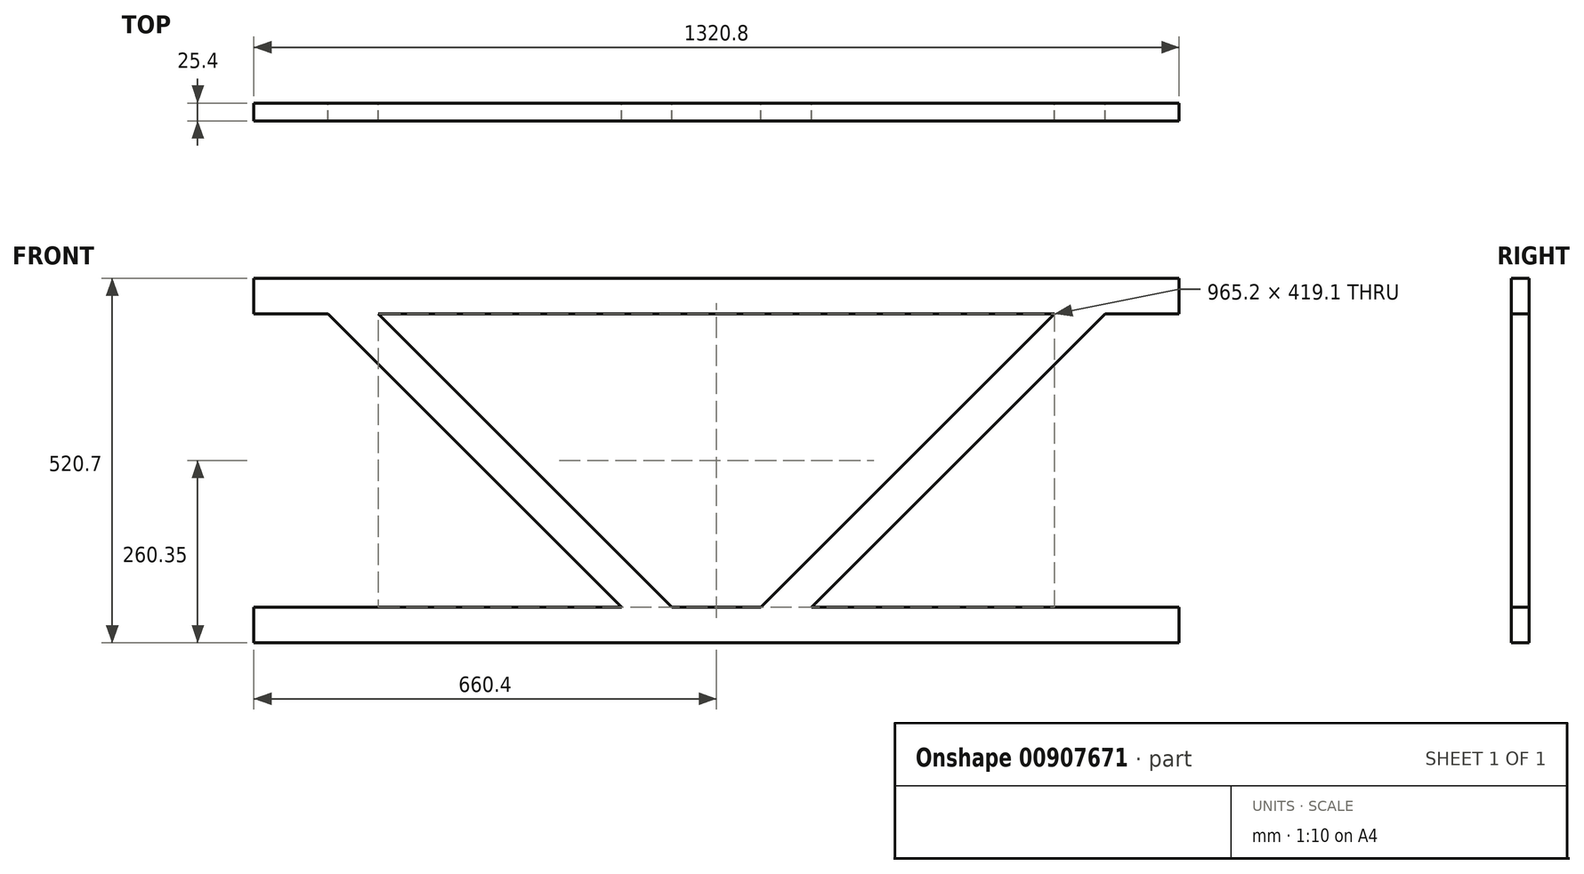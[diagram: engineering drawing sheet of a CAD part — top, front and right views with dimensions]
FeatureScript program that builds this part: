
annotation { "Feature Type Name" : "Feature", "Feature Type Description" : "" }
export const myFeature = defineFeature(function(context is Context, id is Id, definition is map)
    precondition{}
    {
        {
            var Q0;
            Q0=qCreatedBy(makeId("Front.planeOp"),FACE);
            var sketch = newSketch(context, id + "F0", { "sketchPlane" : qUnion([Q0])});
            skLineSegment(sketch, "E0.bottom", {"start": v(660.4, 260.35) * mm, "end": v(-660.4, 260.35) * mm});
            skLineSegment(sketch, "E0.top", {"start": v(660.4, -260.35) * mm, "end": v(-660.4, -260.35) * mm});
            skLineSegment(sketch, "E0.left", {"start": v(660.4, 260.35) * mm, "end": v(660.4, 209.55) * mm});
            skLineSegment(sketch, "E0.right", {"start": v(-660.4, 260.35) * mm, "end": v(-660.4, 209.55) * mm});
            skPoint(sketch, "E0.middle", {"position": v(0, 0) * mm});
            skLineSegment(sketch, "E1.top", {"start": v(660.4, 209.55) * mm, "end": v(63.5, 209.55) * mm});
            skLineSegment(sketch, "E2.top", {"start": v(660.4, -209.55) * mm, "end": v(-660.4, -209.55) * mm});
            skLineSegment(sketch, "E2.left", {"start": v(660.4, -260.35) * mm, "end": v(660.4, -209.55) * mm});
            skLineSegment(sketch, "E2.right", {"start": v(-660.4, -260.35) * mm, "end": v(-660.4, -209.55) * mm});
            skLineSegment(sketch, "E3.trimOffspring", {"start": v(660.4, -209.55) * mm, "end": v(660.4, -260.35) * mm});
            skLineSegment(sketch, "E4.trimOffspring", {"start": v(-660.4, -209.55) * mm, "end": v(-660.4, -260.35) * mm});
            skLineSegment(sketch, "E5.bottom", {"start": v(660.4, -209.55) * mm, "end": v(63.5, -209.55) * mm});
            skLineSegment(sketch, "E6.bottom", {"start": v(-660.4, -209.55) * mm, "end": v(-63.5, -209.55) * mm});
            skLineSegment(sketch, "E6.top", {"start": v(-660.4, 209.55) * mm, "end": v(-63.5, 209.55) * mm});
            skLineSegment(sketch, "E7.trimOffspring", {"start": v(-63.5, 209.55) * mm, "end": v(-660.4, 209.55) * mm});
            skLineSegment(sketch, "E8", {"start": v(63.5, -209.55) * mm, "end": v(482.6, 209.55) * mm});
            skLineSegment(sketch, "E9", {"start": v(-63.5, -209.55) * mm, "end": v(-482.6, 209.55) * mm});
            skLineSegment(sketch, "E10", {"start": v(308.97, -35.92) * mm, "end": v(554.44, 209.55) * mm});
            skLineSegment(sketch, "E11", {"start": v(308.97, -35.92) * mm, "end": v(135.34, -209.55) * mm});
            skLineSegment(sketch, "E12", {"start": v(-308.97, -35.92) * mm, "end": v(-135.34, -209.55) * mm});
            skLineSegment(sketch, "E13", {"start": v(-308.97, -35.92) * mm, "end": v(-554.44, 209.55) * mm});
            skLineSegment(sketch, "E14", {"start": v(-63.5, 209.55) * mm, "end": v(63.5, 209.55) * mm});
            skPoint(sketch, "E15.start.orphan", {"position": v(273.05, 0) * mm});
            skPoint(sketch, "E16.start.orphan", {"position": v(-273.05, 0) * mm});
            skSolve(sketch);
        }
        {
            var Q0;
            Q0=makeQuery(id+"F0.imprint","IMPRINT",FACE,{"disambiguationData":[TD([[makeQuery(id+"F0.imprint","IMPRINT",EDGE,{"derivedFrom":sQuery(id+"F0.wireOp",EDGE,"E0.bottom")}),1.0]])]});
            var Q1;
            {var subQ1=sQuery(id+"F0.wireOp",EDGE,"E8");Q1=makeQuery(id+"F0.imprint","IMPRINT",FACE,{"disambiguationData":[TD([[makeQuery(id+"F0.imprint","IMPRINT",EDGE,{"derivedFrom":subQ1}),-1.0]])]});}
            var Q2;
            Q2=makeQuery(id+"F0.imprint","IMPRINT",FACE,{"disambiguationData":[TD([[makeQuery(id+"F0.imprint","IMPRINT",EDGE,{"derivedFrom":sQuery(id+"F0.wireOp",EDGE,"E0.top")}),-1.0]])]});
            var Q3;
            {var subQ0=sQuery(id+"F0.wireOp",EDGE,"E9");Q3=makeQuery(id+"F0.imprint","IMPRINT",FACE,{"disambiguationData":[TD([[makeQuery(id+"F0.imprint","IMPRINT",EDGE,{"derivedFrom":subQ0}),1.0]])]});}
            extrude(context, id + "F1", {"entities" : qUnion([Q0, Q1, Q2, Q3]), "depth" : 25.4 * mm, "offsetDistance" : 25.4 * mm});
        }
    });
